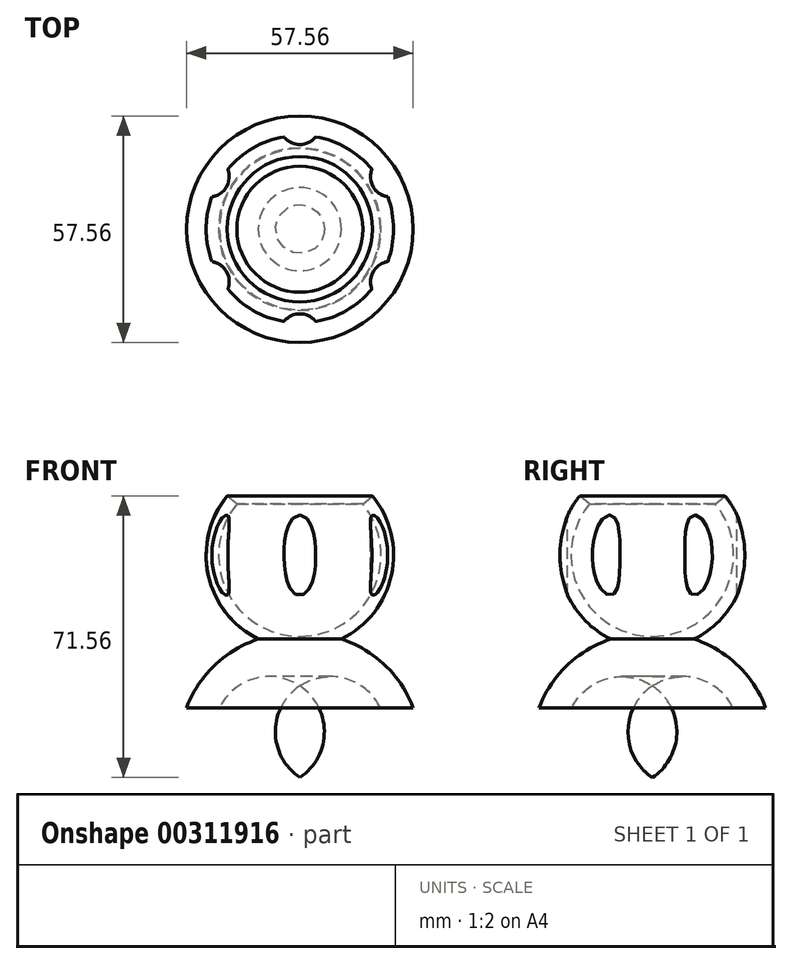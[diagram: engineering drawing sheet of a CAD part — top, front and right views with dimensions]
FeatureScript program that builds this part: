
annotation { "Feature Type Name" : "Feature", "Feature Type Description" : "" }
export const myFeature = defineFeature(function(context is Context, id is Id, definition is map)
    precondition{}
    {
        {
            var Q0;
            Q0=qCreatedBy(makeId("Right.planeOp"),FACE);
            var sketch = newSketch(context, id + "F0", { "sketchPlane" : qUnion([Q0])});
            skArc(sketch, "E0", {"start": v(0, -23.8) * mm, "mid": v(21.5, -10.21) * mm, "end": v(18.45, 15.05) * mm});
            skArc(sketch, "E1", {"start": v(28.78, -38.78) * mm, "mid": v(21.67, -27.97) * mm, "end": v(10.57, -21.33) * mm});
            skLineSegment(sketch, "E2", {"start": v(28.78, -38.78) * mm, "end": v(20.43, -38.78) * mm});
            skArc(sketch, "E3", {"start": v(20.43, -38.78) * mm, "mid": v(11.49, -31.33) * mm, "end": v(0, -33.21) * mm});
            skLineSegment(sketch, "E4", {"start": v(0, -33.21) * mm, "end": v(0, 42.16) * mm});
            skArc(sketch, "E5.0", {"start": v(0, -20.63) * mm, "mid": v(18.64, -8.85) * mm, "end": v(16, 13.04) * mm});
            skLineSegment(sketch, "E6", {"start": v(16, 13.04) * mm, "end": v(18.45, 15.05) * mm});
            skSolve(sketch);
        }
        {
            var Q0;
            {var subQ0=sQuery(id+"F0.wireOp",EDGE,"E5.0");Q0=makeQuery(id+"F0.imprint","IMPRINT",FACE,{"disambiguationData":[TD([[makeQuery(id+"F0.imprint","IMPRINT",EDGE,{"derivedFrom":subQ0}),-1.0]])]});}
            var Q1;
            {var subQ1=sQuery(id+"F0.wireOp",EDGE,"E1");Q1=makeQuery(id+"F0.imprint","IMPRINT",FACE,{"disambiguationData":[TD([[makeQuery(id+"F0.imprint","IMPRINT",EDGE,{"derivedFrom":subQ1}),1.0]])]});}
            var Q2;
            Q2=sQuery(id+"F0.wireOp",EDGE,"E4");
            revolve(context, id + "F1", {"entities" : qUnion([Q0, Q1]), "axis" : qUnion([Q2]), "revolveType" : RevolveType.FULL});
        }
        {
            var Q0;
            Q0=qCreatedBy(makeId("Top.planeOp"),FACE);
            cPlane(context, id + "F2", {"entities" : qUnion([Q0]), "cplaneType" : CPlaneType.OFFSET, "offset" : 50.8 * mm, "width" : 152.4 * mm, "height" : 152.4 * mm});
        }
        {
            var Q0;
            Q0=qCreatedBy(id+"F2.planeOp",FACE);
            var sketch = newSketch(context, id + "F3", { "sketchPlane" : qUnion([Q0])});
            skCircle(sketch, "E7", {"center": v(0, 26.67) * mm, "radius": 5.16 * mm});
            skCircle(sketch, "E8.1.0", {"center": v(-23.1, 13.34) * mm, "radius": 5.16 * mm});
            skCircle(sketch, "E8.2.0", {"center": v(-23.1, -13.33) * mm, "radius": 5.16 * mm});
            skCircle(sketch, "E8.3.0", {"center": v(0, -26.67) * mm, "radius": 5.16 * mm});
            skCircle(sketch, "E8.4.0", {"center": v(23.1, -13.34) * mm, "radius": 5.16 * mm});
            skCircle(sketch, "E8.5.0", {"center": v(23.1, 13.34) * mm, "radius": 5.16 * mm});
            skPoint(sketch, "E8.center", {"position": v(0, 0) * mm});
            skSolve(sketch);
        }
        {
            var Q0;
            Q0=makeQuery(id+"F3.imprint","IMPRINT",FACE,{"disambiguationData":[TD([[makeQuery(id+"F3.imprint","IMPRINT",EDGE,{"derivedFrom":sQuery(id+"F3.wireOp",EDGE,"E7")}),1.0]])]});
            var Q1;
            Q1=makeQuery(id+"F3.imprint","IMPRINT",FACE,{"disambiguationData":[TD([[makeQuery(id+"F3.imprint","IMPRINT",EDGE,{"derivedFrom":sQuery(id+"F3.wireOp",EDGE,"E8.1.0")}),1.0]])]});
            var Q2;
            Q2=makeQuery(id+"F3.imprint","IMPRINT",FACE,{"disambiguationData":[TD([[makeQuery(id+"F3.imprint","IMPRINT",EDGE,{"derivedFrom":sQuery(id+"F3.wireOp",EDGE,"E8.2.0")}),1.0]])]});
            var Q3;
            Q3=makeQuery(id+"F3.imprint","IMPRINT",FACE,{"disambiguationData":[TD([[makeQuery(id+"F3.imprint","IMPRINT",EDGE,{"derivedFrom":sQuery(id+"F3.wireOp",EDGE,"E8.4.0")}),1.0]])]});
            var Q4;
            Q4=makeQuery(id+"F3.imprint","IMPRINT",FACE,{"disambiguationData":[TD([[makeQuery(id+"F3.imprint","IMPRINT",EDGE,{"derivedFrom":sQuery(id+"F3.wireOp",EDGE,"E8.5.0")}),1.0]])]});
            var Q5;
            Q5=makeQuery(id+"F3.imprint","IMPRINT",FACE,{"disambiguationData":[TD([[makeQuery(id+"F3.imprint","IMPRINT",EDGE,{"derivedFrom":sQuery(id+"F3.wireOp",EDGE,"E8.3.0")}),1.0]])]});
            extrude(context, id + "F4", {"entities" : qUnion([Q0, Q1, Q2, Q3, Q4, Q5]), "operationType" : NewBodyOperationType.REMOVE, "oppositeDirection" : true, "depth" : 63.5 * mm});
        }
    });
